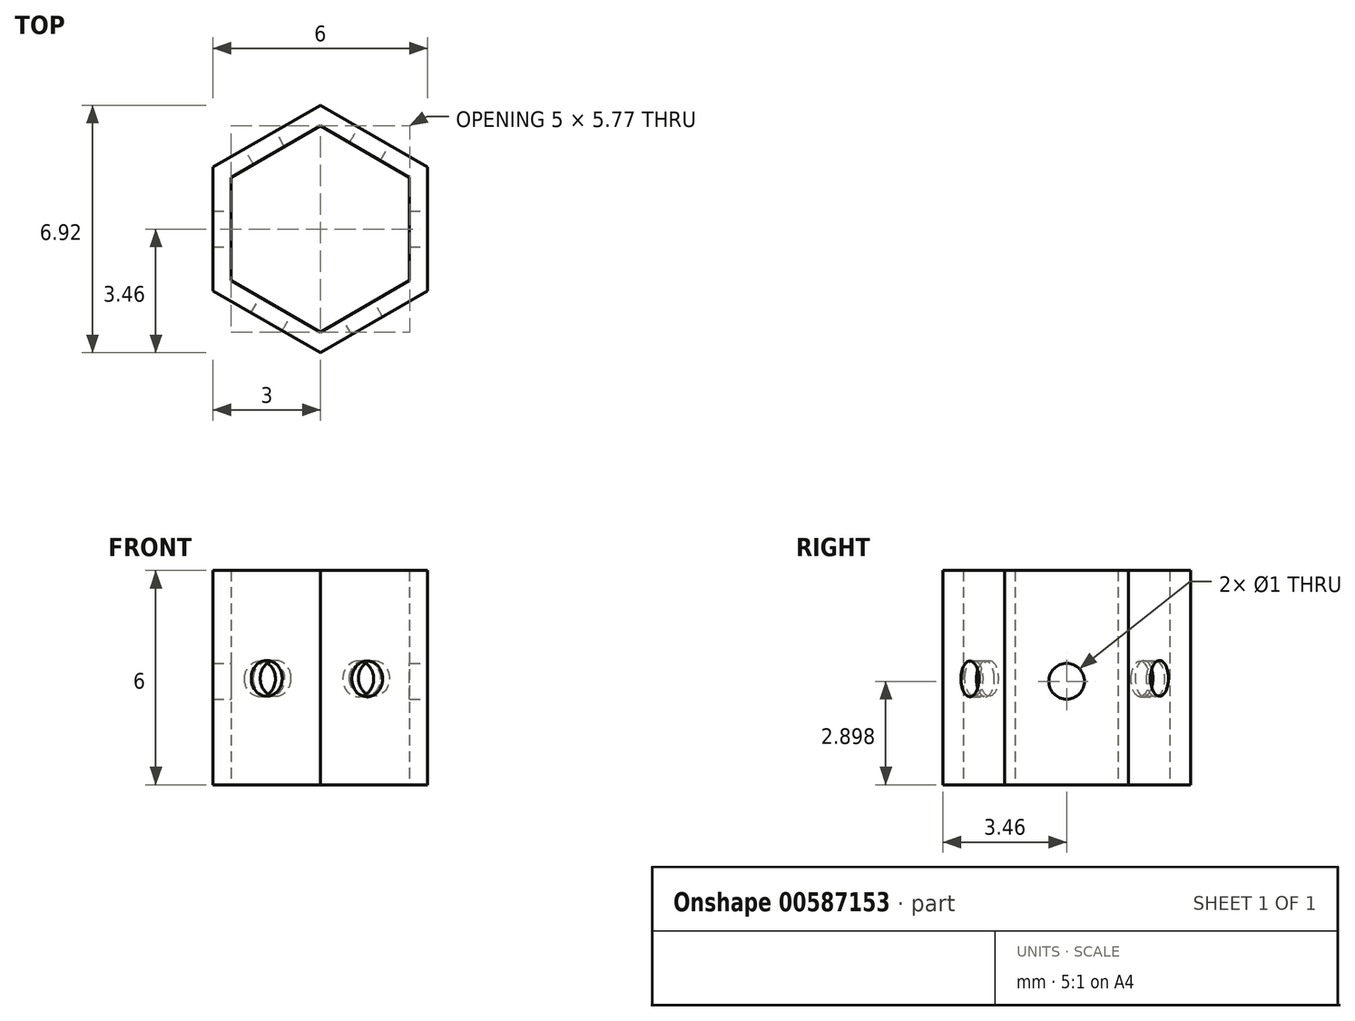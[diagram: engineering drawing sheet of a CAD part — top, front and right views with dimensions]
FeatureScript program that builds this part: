
annotation { "Feature Type Name" : "Feature", "Feature Type Description" : "" }
export const myFeature = defineFeature(function(context is Context, id is Id, definition is map)
    precondition{}
    {
        {
            var Q0;
            Q0=qCreatedBy(makeId("Top.planeOp"),FACE);
            var sketch = newSketch(context, id + "F0", { "sketchPlane" : qUnion([Q0])});
            skCircle(sketch, "E0.cCircle", {"center": v(0, 0) * mm, "radius": 3 * mm, "construction": true});
            skLineSegment(sketch, "E0.0", {"start": v(-3, -1.73) * mm, "end": v(-3, 1.73) * mm});
            skLineSegment(sketch, "E0.1", {"start": v(-3, 1.73) * mm, "end": v(0, 3.46) * mm});
            skLineSegment(sketch, "E0.2", {"start": v(0, 3.46) * mm, "end": v(3, 1.73) * mm});
            skLineSegment(sketch, "E0.3", {"start": v(3, 1.73) * mm, "end": v(3, -1.73) * mm});
            skLineSegment(sketch, "E0.4", {"start": v(3, -1.73) * mm, "end": v(0, -3.46) * mm});
            skLineSegment(sketch, "E0.5", {"start": v(0, -3.46) * mm, "end": v(-3, -1.73) * mm});
            skPoint(sketch, "E0.0.midPoint", {"position": v(-3, 0) * mm});
            skCircle(sketch, "E1.cCircle", {"center": v(0, 0) * mm, "radius": 2.5 * mm, "construction": true});
            skLineSegment(sketch, "E1.0", {"start": v(-2.5, -1.44) * mm, "end": v(-2.5, 1.44) * mm});
            skLineSegment(sketch, "E1.1", {"start": v(-2.5, 1.44) * mm, "end": v(0, 2.89) * mm});
            skLineSegment(sketch, "E1.2", {"start": v(0, 2.89) * mm, "end": v(2.5, 1.44) * mm});
            skLineSegment(sketch, "E1.3", {"start": v(2.5, 1.44) * mm, "end": v(2.5, -1.44) * mm});
            skLineSegment(sketch, "E1.4", {"start": v(2.5, -1.44) * mm, "end": v(0, -2.89) * mm});
            skLineSegment(sketch, "E1.5", {"start": v(0, -2.89) * mm, "end": v(-2.5, -1.44) * mm});
            skPoint(sketch, "E1.0.midPoint", {"position": v(-2.5, 0) * mm});
            skSolve(sketch);
        }
        {
            var Q0;
            Q0=makeQuery(id+"F0.imprint","IMPRINT",FACE,{"disambiguationData":[TD([[makeQuery(id+"F0.imprint","IMPRINT",EDGE,{"derivedFrom":sQuery(id+"F0.wireOp",EDGE,"E0.0")}),-1.0]])]});
            extrude(context, id + "F1", {"entities" : qUnion([Q0]), "depth" : 6 * mm, "offsetDistance" : 25 * mm});
        }
        {
            var Q0;
            Q0=makeQuery(id+"F1.opExtrude","SWEPT_FACE",FACE,{"disambiguationData":[OSD([sQuery(id+"F0.wireOp",EDGE,"E0.3")])]});
            var sketch = newSketch(context, id + "F2", { "sketchPlane" : qUnion([Q0])});
            skCircle(sketch, "E2", {"center": v(0, 2.9) * mm, "radius": 0.5 * mm});
            skSolve(sketch);
        }
        {
            var Q0;
            Q0=makeQuery(id+"F2.imprint","IMPRINT",FACE,{"disambiguationData":[TD([[makeQuery(id+"F2.imprint","IMPRINT",EDGE,{"derivedFrom":sQuery(id+"F2.wireOp",EDGE,"E2")}),1.0]])]});
            extrude(context, id + "F3", {"entities" : qUnion([Q0]), "operationType" : NewBodyOperationType.REMOVE, "oppositeDirection" : true, "depth" : 10 * mm, "offsetDistance" : 25 * mm});
        }
        {
            var Q0;
            Q0=makeQuery(id+"F1.opExtrude","SWEPT_FACE",FACE,{"disambiguationData":[OSD([sQuery(id+"F0.wireOp",EDGE,"E0.2")])]});
            var sketch = newSketch(context, id + "F4", { "sketchPlane" : qUnion([Q0])});
            skCircle(sketch, "E3", {"center": v(0, 2.98) * mm, "radius": 0.5 * mm});
            skSolve(sketch);
        }
        {
            var Q0;
            Q0 = qSketchRegion(id + "F4", true);
            extrude(context, id + "F5", {"entities" : qUnion([Q0]), "operationType" : NewBodyOperationType.REMOVE, "oppositeDirection" : true, "depth" : 10 * mm, "offsetDistance" : 25 * mm});
        }
        {
            var Q0;
            Q0=makeQuery(id+"F1.opExtrude","SWEPT_FACE",FACE,{"disambiguationData":[OSD([sQuery(id+"F0.wireOp",EDGE,"E0.1")])]});
            var sketch = newSketch(context, id + "F6", { "sketchPlane" : qUnion([Q0])});
            skCircle(sketch, "E4", {"center": v(0.22, 2.97) * mm, "radius": 0.5 * mm});
            skSolve(sketch);
        }
        {
            var Q0;
            Q0=makeQuery(id+"F6.imprint","IMPRINT",FACE,{"disambiguationData":[TD([[makeQuery(id+"F6.imprint","IMPRINT",EDGE,{"derivedFrom":sQuery(id+"F6.wireOp",EDGE,"E4")}),1.0]])]});
            extrude(context, id + "F7", {"entities" : qUnion([Q0]), "operationType" : NewBodyOperationType.REMOVE, "oppositeDirection" : true, "depth" : 10 * mm, "offsetDistance" : 25 * mm});
        }
    });
